# Revit family: Keilhauer-Epix-Stool-
name_source: partatom
category: Furniture
revit_build: Autodesk Revit 2016 (Build: 20150220_1215(x64)
units: mm (PartAtom-declared; Revit-internal decimal feet)

## family parameters
Always vertical = Yes
Cut with Voids When Loaded = No
OmniClass Number = 23.40.70.14.64.11
OmniClass Title = Office Furniture
Room Calculation Point = No
Shared = No
Work Plane-Based = No

## types (6) — shared parameters
Assembly Code = E2020200
Catalog = EPIX
Keilhauer Epix Seat Pad = <By Category>
Manufacturer = Keilhauer, Corp.
Product Documentation Link = https://keilhauer.com
URL = http://www.keilhauer.com

## per-type parameters (varying)
| type | Arms | Description | Revit Model Built By | Seat Pad |
| 76205 | No | Epix counter stool, plastic shell, sled base | https://servex-us.com | No |
| 76215 | No | Epix counter stool, formed felt shell, sled base |  | No |
| 76225 | No | Epix counter stool, plastic shell with seat pad, sled base |  | Yes |
| 76235 | Yes | Epix counter stool, plastic shell with arms, sled base |  | No |
| 76245 | Yes | Epix counter stool, formed felt shell with arms, sled base |  | No |
| 76255 | Yes | Epix counter stool, plastic shell with arms and seat pad, sled base |  | Yes |

note: column(s) folded — value = type name in every type: Model

## geometry (parser evidence)
native form markers: Sweep x5
no freeform markers — native parametric forms only
